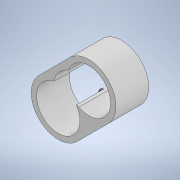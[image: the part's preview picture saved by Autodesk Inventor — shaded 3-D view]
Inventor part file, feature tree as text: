
AUTODESK INVENTOR PART (.ipt)
format: ipt  version: 2020 (Build 240168000, 168)  size: 211,456 bytes
history: native  units: in
note: dims shown in document units (in); Inventor stores cm internally (conversion verified against a paired STEP export)
features: extrude x4, sketch x4, fillet x2
ambient origin geometry x8: Origin, YZ Plane, XZ Plane, XY Plane, X Axis, Y Axis, Z Axis, Center Point
bodies: Solid1 (feature_tree)
feature tree (10):
  extrude  "Extrusion1"  Depth=0.9606in
  extrude  "Extrusion3"  TaperAngle=45.0deg  [1 undecoded]
  extrude  "Extrusion4"  Depth=0.4134in
  extrude  "Extrusion5"  Depth=0.1181in
  fillet  "Fillet1"  Radius=0.1181in
  fillet  "Fillet2"  Radius=0.1181in
  sketch  "Sketch1"  dims[d0=0.9724in d1=0.9606in]
  sketch  "Sketch3"  dims[d2=0.0in d3=45.0deg]
  sketch  "Sketch4"  dims[d4=0.0in d5=0.4134in]
  sketch  "Sketch5"  dims[d20=0.3346in d21=0.1181in d22=0.1181in d23=0.1181in d24=0.9606in d25=0.9606in d26=0.1772in d27=0.1181in d28=0.0in d32=0.9724in d33=0.9606in d34=0.0in d35=45.0deg d36=0.0in d37=0.4134in d38=0.3346in d39=0.1181in d40=0.1181in d41=0.1181in d42=0.9606in d43=0.9606in d44=0.1772in d45=0.6102in d46=0.0in d49=0.2165in d50=0.0787in d51=0.0394in d52=0.0in d53=0.0in d54=0.9724in d55=0.9606in d56=0.0in d57=45.0deg d58=0.0in d59=0.4134in d60=0.3346in d61=0.1181in d62=0.1181in d63=0.1181in d64=0.9606in d65=0.9606in d66=0.1772in d67=0.5984in d68=0.5984in d69=1.1969in d70=0.5984in d71=0.7283in d72=0.0in d73=0.1181in d74=0.1181in]
note: 1 required parameter value undecoded (feature->parameter linkage not recoverable at this tier; creation-order binding heuristic only, values carry confidence <= 0.55)
